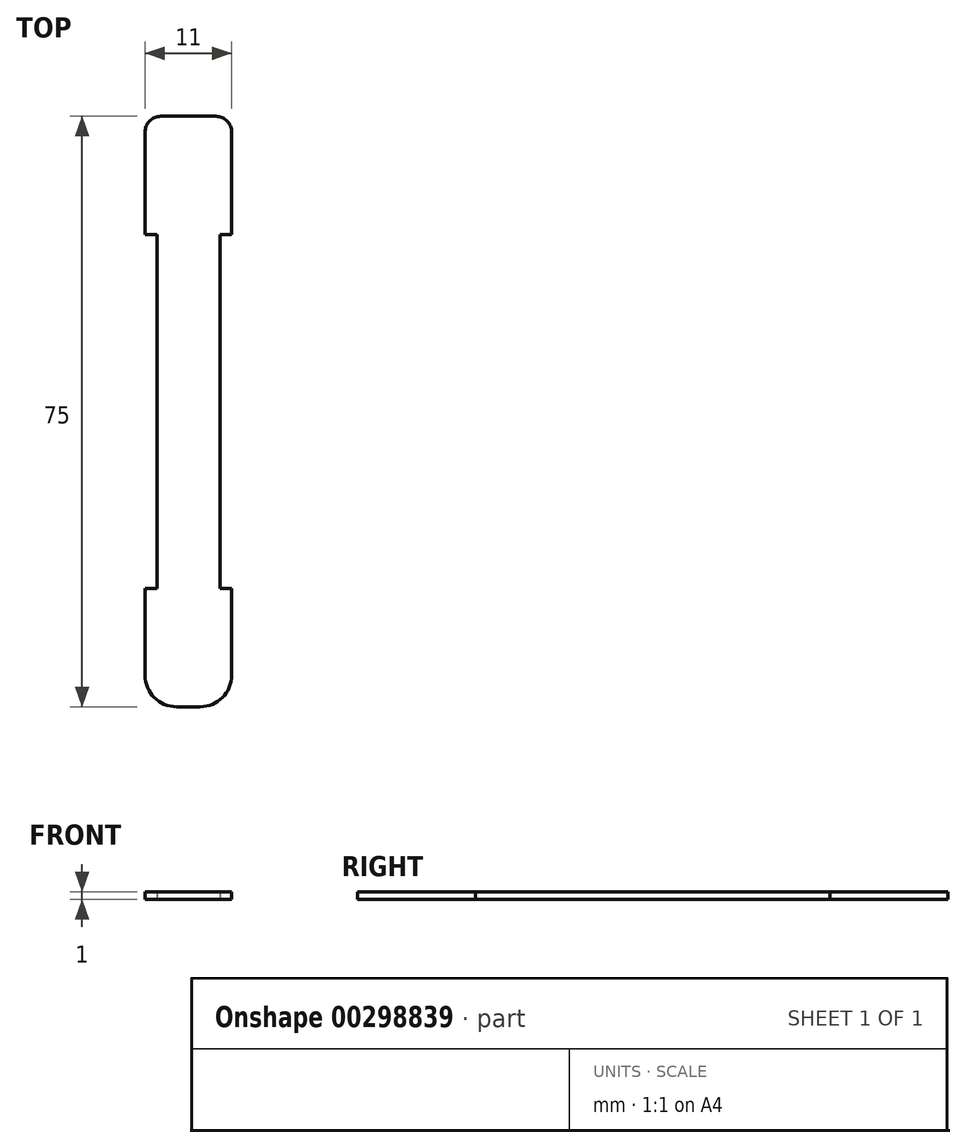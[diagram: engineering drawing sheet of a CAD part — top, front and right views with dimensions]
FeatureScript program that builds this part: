
annotation { "Feature Type Name" : "Feature", "Feature Type Description" : "" }
export const myFeature = defineFeature(function(context is Context, id is Id, definition is map)
    precondition{}
    {
        {
            var Q0;
            Q0=qCreatedBy(makeId("Top.planeOp"),FACE);
            var sketch = newSketch(context, id + "F0", { "sketchPlane" : qUnion([Q0])});
            skLineSegment(sketch, "E0.bottom", {"start": v(3.5, 37.5) * mm, "end": v(-3.5, 37.5) * mm});
            skLineSegment(sketch, "E0.top", {"start": v(1.5, -37.5) * mm, "end": v(-1.5, -37.5) * mm});
            skLineSegment(sketch, "E0.left", {"start": v(5.5, 35.5) * mm, "end": v(5.5, 22.5) * mm});
            skLineSegment(sketch, "E0.right", {"start": v(-5.5, 35.5) * mm, "end": v(-5.5, 22.5) * mm});
            skPoint(sketch, "E0.middle", {"position": v(0, 0) * mm});
            skLineSegment(sketch, "E1", {"start": v(-5.5, 22.5) * mm, "end": v(-4, 22.5) * mm});
            skLineSegment(sketch, "E2", {"start": v(-5.5, -22.5) * mm, "end": v(-4, -22.5) * mm});
            skLineSegment(sketch, "E3", {"start": v(-4, 22.5) * mm, "end": v(-4, -22.5) * mm});
            skLineSegment(sketch, "E4", {"start": v(4, 22.5) * mm, "end": v(4, -22.5) * mm});
            skPoint(sketch, "E5.orphan", {"position": v(0, 37.5) * mm});
            skLineSegment(sketch, "E6.trimOffspring", {"start": v(4, 22.5) * mm, "end": v(5.5, 22.5) * mm});
            skLineSegment(sketch, "E7.trimOffspring", {"start": v(-5.5, -22.5) * mm, "end": v(-5.5, -33.5) * mm});
            skLineSegment(sketch, "E8.trimOffspring", {"start": v(4, -22.5) * mm, "end": v(5.5, -22.5) * mm});
            skPoint(sketch, "E9.end.orphan", {"position": v(0, -37.5) * mm});
            skLineSegment(sketch, "E10.trimOffspring", {"start": v(5.5, -22.5) * mm, "end": v(5.5, -33.5) * mm});
            skPoint(sketch, "E11.visualSharp", {"position": v(-5.5, 37.5) * mm});
            skArc(sketch, "E11.filletArc", {"start": v(-3.5, 37.5) * mm, "mid": v(-4.91, 36.91) * mm, "end": v(-5.5, 35.5) * mm});
            skPoint(sketch, "E12.visualSharp", {"position": v(5.5, 37.5) * mm});
            skArc(sketch, "E12.filletArc", {"start": v(5.5, 35.5) * mm, "mid": v(4.91, 36.91) * mm, "end": v(3.5, 37.5) * mm});
            skPoint(sketch, "E13.visualSharp", {"position": v(-5.5, -37.5) * mm});
            skArc(sketch, "E13.filletArc", {"start": v(-5.5, -33.5) * mm, "mid": v(-4.33, -36.33) * mm, "end": v(-1.5, -37.5) * mm});
            skPoint(sketch, "E14.visualSharp", {"position": v(5.5, -37.5) * mm});
            skArc(sketch, "E14.filletArc", {"start": v(1.5, -37.5) * mm, "mid": v(4.33, -36.33) * mm, "end": v(5.5, -33.5) * mm});
            skSolve(sketch);
        }
        {
            var Q0;
            Q0=makeQuery(id+"F0.imprint","IMPRINT",FACE,{"disambiguationData":[TD([[makeQuery(id+"F0.imprint","IMPRINT",EDGE,{"derivedFrom":sQuery(id+"F0.wireOp",EDGE,"E0.bottom")}),1.0]])]});
            extrude(context, id + "F1", {"entities" : qUnion([Q0]), "depth" : 1 * mm});
        }
    });
